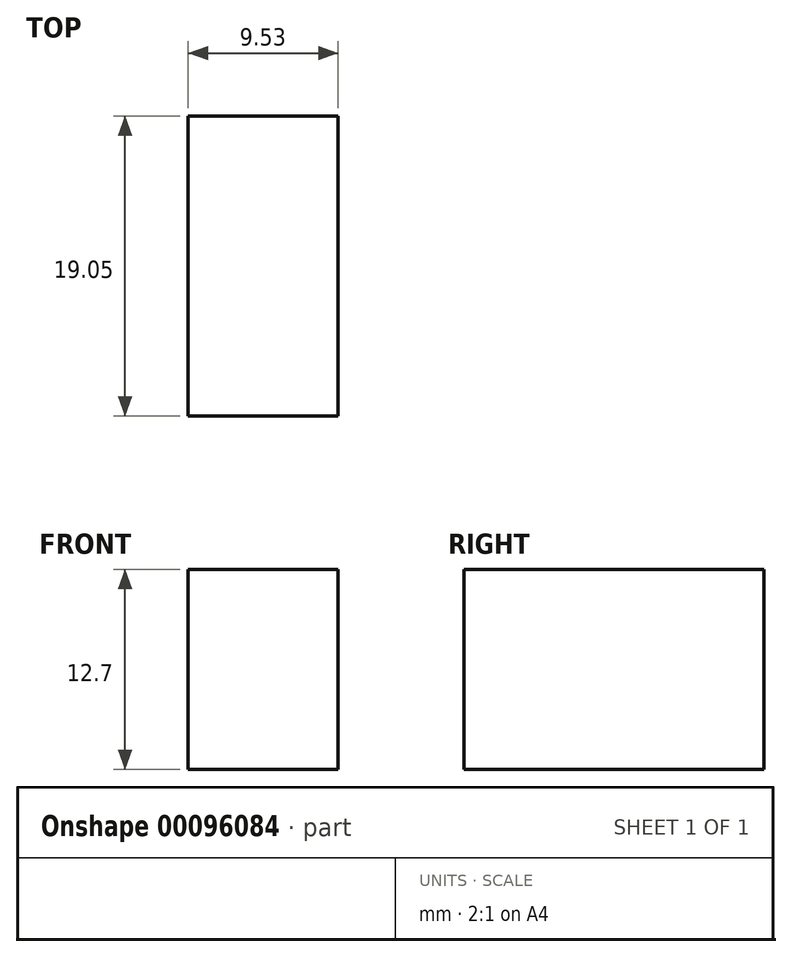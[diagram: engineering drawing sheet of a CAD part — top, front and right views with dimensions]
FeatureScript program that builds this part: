
annotation { "Feature Type Name" : "Feature", "Feature Type Description" : "" }
export const myFeature = defineFeature(function(context is Context, id is Id, definition is map)
    precondition{}
    {
        {
            var Q0;
            Q0=qCreatedBy(makeId("Front.planeOp"),FACE);
            var sketch = newSketch(context, id + "F0", { "sketchPlane" : qUnion([Q0])});
            skLineSegment(sketch, "E0.bottom", {"start": v(0, 0) * mm, "end": v(9.53, 0) * mm});
            skLineSegment(sketch, "E0.top", {"start": v(0, 12.7) * mm, "end": v(9.52, 12.7) * mm});
            skLineSegment(sketch, "E0.left", {"start": v(0, 0) * mm, "end": v(0, 12.7) * mm});
            skLineSegment(sketch, "E0.right", {"start": v(9.53, 0) * mm, "end": v(9.52, 12.7) * mm});
            skSolve(sketch);
        }
        {
            var Q0;
            Q0=makeQuery(id+"F0.imprint","IMPRINT",FACE,{"disambiguationData":[TD([[makeQuery(id+"F0.imprint","IMPRINT",EDGE,{"derivedFrom":sQuery(id+"F0.wireOp",EDGE,"E0.bottom")}),1.0]])]});
            extrude(context, id + "F1", {"entities" : qUnion([Q0]), "depth" : 19.05 * mm});
        }
    });
